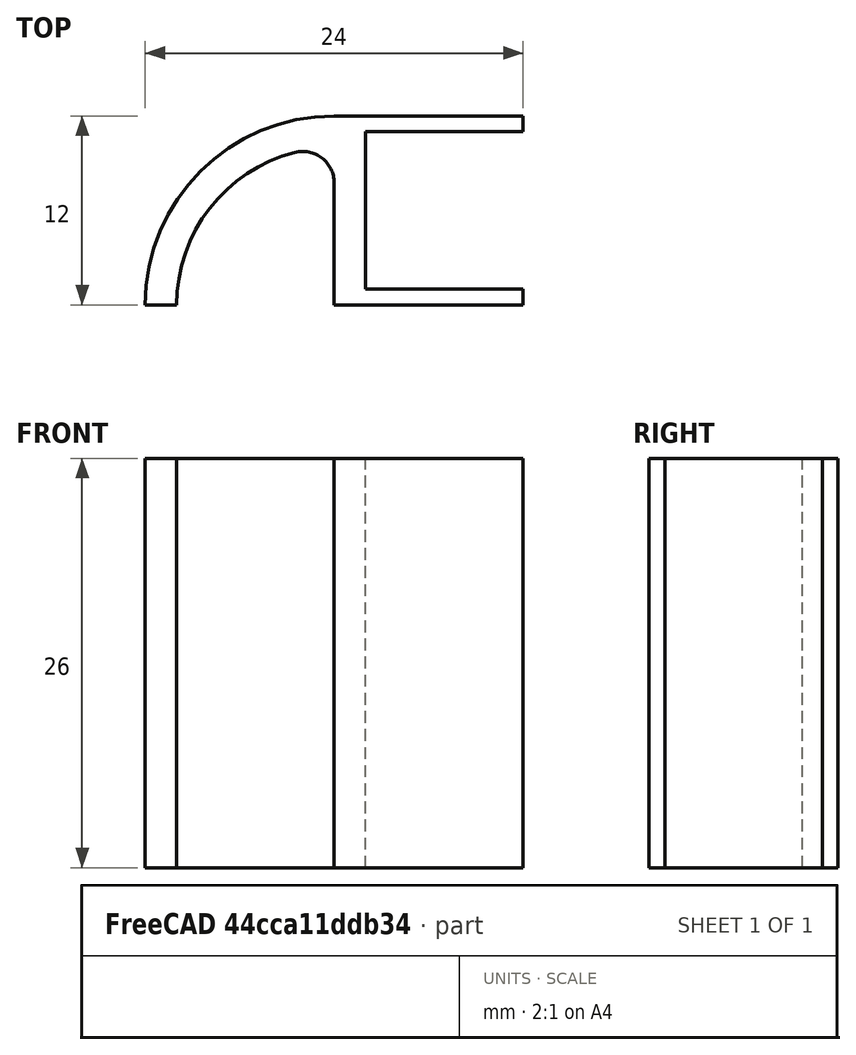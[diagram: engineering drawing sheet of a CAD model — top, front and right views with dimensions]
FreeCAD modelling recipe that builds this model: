
FCSTD DOCUMENT  (FreeCAD 0.19R24366 (Git))
Label: ramp_for_tape
License: All rights reserved
LicenseURL: http://en.wikipedia.org/wiki/All_rights_reserved
objects: Part::Box×2, Part::Cylinder×2, Part::Cut×2, Part::MultiFuse×1, Part::Fillet×1
note: 8 computed .brp shape members not serialized (recipe doc carries the construction recipe); baked Part::Feature solids carry a one-line shape summary decoded from their .brp

FEATURE [Part::Box] Box  label="Cube"
  AttacherType = Attacher::AttachEngine3D
  Height = 26
  Length = 12
  Width = 12
FEATURE [Part::Box] Box001  label="Cube001"
  AttacherType = Attacher::AttachEngine3D
  Height = 26
  Length = 10
  Placement = pos=(2,1,0) rot=(0,0,1;0rad)
  Width = 10
FEATURE [Part::Cylinder] Cylinder
  Angle = 90
  AttacherType = Attacher::AttachEngine3D
  Height = 26
  Placement = pos=(0,0,0) rot=(0,0,1;1.5708rad)
  Radius = 12
FEATURE [Part::MultiFuse] Fusion
  Shapes = -> [Box,Cylinder]
FEATURE [Part::Cut] Cut
  Base = -> Fusion
  Tool = -> Box001
FEATURE [Part::Cylinder] Cylinder001
  Angle = 90
  AttacherType = Attacher::AttachEngine3D
  Height = 26
  Placement = pos=(0,0,0) rot=(0,0,1;1.5708rad)
  Radius = 10
FEATURE [Part::Cut] Cut001
  Base = -> Cut
  Tool = -> Cylinder001
FEATURE [Part::Fillet] Fillet
  Base = -> Cut001
  Edges = 1 edges r=2: [Edge23]
